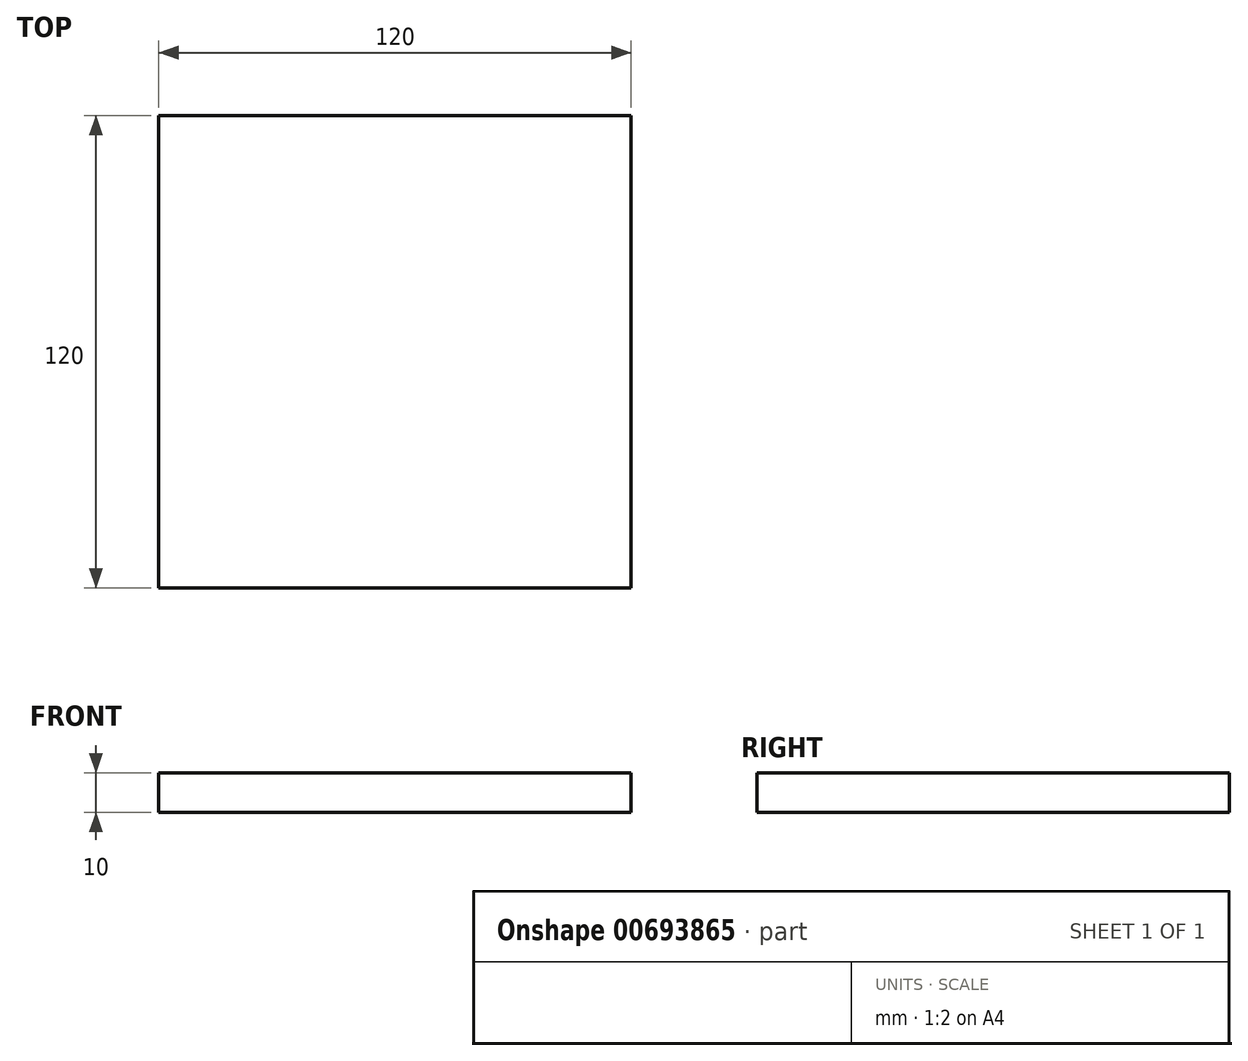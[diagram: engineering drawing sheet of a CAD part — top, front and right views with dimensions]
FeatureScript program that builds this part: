
annotation { "Feature Type Name" : "Feature", "Feature Type Description" : "" }
export const myFeature = defineFeature(function(context is Context, id is Id, definition is map)
    precondition{}
    {
        {
            var Q0;
            Q0=qCreatedBy(makeId("Top.planeOp"),FACE);
            var sketch = newSketch(context, id + "F0", { "sketchPlane" : qUnion([Q0])});
            skLineSegment(sketch, "E0.bottom", {"start": v(60, -60) * mm, "end": v(-60, -60) * mm});
            skLineSegment(sketch, "E0.top", {"start": v(60, 60) * mm, "end": v(-60, 60) * mm});
            skLineSegment(sketch, "E0.left", {"start": v(60, -60) * mm, "end": v(60, 60) * mm});
            skLineSegment(sketch, "E0.right", {"start": v(-60, -60) * mm, "end": v(-60, 60) * mm});
            skPoint(sketch, "E0.middle", {"position": v(0, 0) * mm});
            skLineSegment(sketch, "E1.bottom", {"start": v(60, -60) * mm, "end": v(-50, -60) * mm});
            skLineSegment(sketch, "E1.left", {"start": v(60, -60) * mm, "end": v(60, 50) * mm});
            skSolve(sketch);
        }
        {
            var Q0;
            Q0=makeQuery(id+"F0.imprint","IMPRINT",FACE,{"disambiguationData":[TD([[makeQuery(id+"F0.imprint","IMPRINT",EDGE,{"derivedFrom":sQuery(id+"F0.wireOp",EDGE,"E0.bottom")}),-1.0]])]});
            extrude(context, id + "F1", {"entities" : qUnion([Q0]), "depth" : 10 * mm, "offsetDistance" : 25 * mm});
        }
    });
